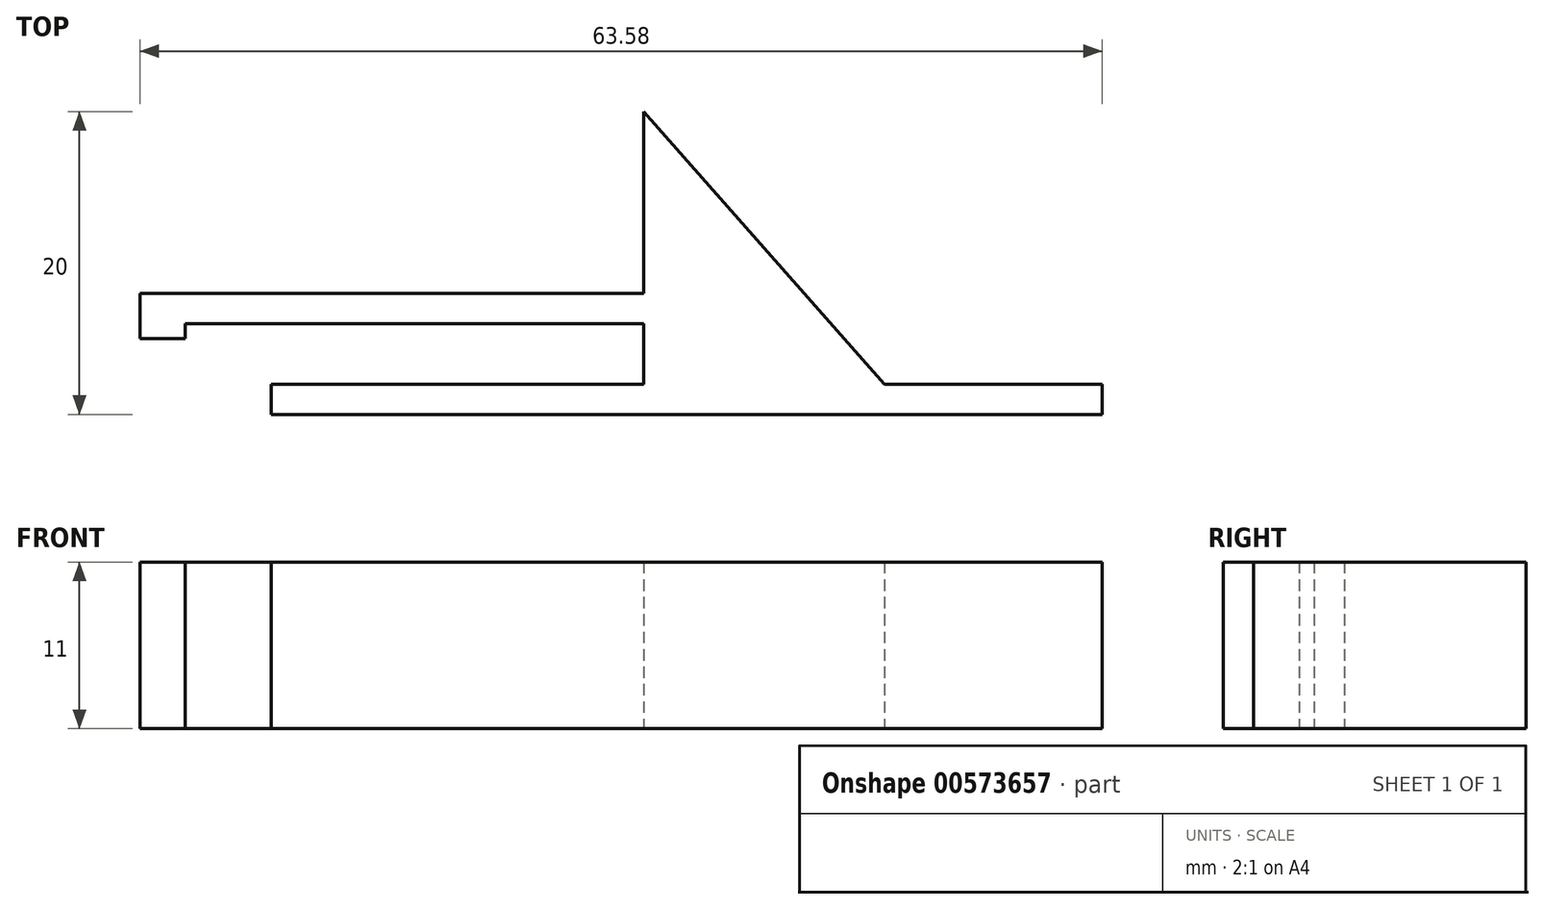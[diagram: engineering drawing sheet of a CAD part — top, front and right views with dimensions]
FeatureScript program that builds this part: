
annotation { "Feature Type Name" : "Feature", "Feature Type Description" : "" }
export const myFeature = defineFeature(function(context is Context, id is Id, definition is map)
    precondition{}
    {
        {
            var Q0;
            Q0=qCreatedBy(makeId("Top.planeOp"),FACE);
            var sketch = newSketch(context, id + "F0", { "sketchPlane" : qUnion([Q0])});
            skLineSegment(sketch, "E0", {"start": v(-24.6, 12.27) * mm, "end": v(30.32, 12.27) * mm});
            skLineSegment(sketch, "E1", {"start": v(30.32, 12.27) * mm, "end": v(30.32, 14.27) * mm});
            skLineSegment(sketch, "E2", {"start": v(30.5, 14.27) * mm, "end": v(15.9, 14.27) * mm});
            skLineSegment(sketch, "E3", {"start": v(-24.6, 12.27) * mm, "end": v(-24.6, 14.27) * mm});
            skLineSegment(sketch, "E4", {"start": v(-24.6, 14.27) * mm, "end": v(0, 14.27) * mm});
            skLineSegment(sketch, "E5", {"start": v(0, 14.27) * mm, "end": v(0, 18.27) * mm});
            skLineSegment(sketch, "E6", {"start": v(0, 18.27) * mm, "end": v(-30.26, 18.27) * mm});
            skLineSegment(sketch, "E7", {"start": v(-30.26, 18.27) * mm, "end": v(-30.26, 17.27) * mm});
            skLineSegment(sketch, "E8", {"start": v(-30.26, 17.27) * mm, "end": v(-33.26, 17.27) * mm});
            skLineSegment(sketch, "E9", {"start": v(-33.26, 17.27) * mm, "end": v(-33.26, 20.27) * mm});
            skLineSegment(sketch, "E10", {"start": v(-33.26, 20.27) * mm, "end": v(0, 20.27) * mm});
            skLineSegment(sketch, "E11", {"start": v(0, 20.27) * mm, "end": v(0, 32.27) * mm});
            skLineSegment(sketch, "E12", {"start": v(0, 32.27) * mm, "end": v(15.9, 14.27) * mm});
            skSolve(sketch);
        }
        {
            var Q0;
            Q0 = qSketchRegion(id + "F0", true);
            extrude(context, id + "F1", {"entities" : qUnion([Q0]), "depth" : 11 * mm, "offsetDistance" : 25 * mm});
        }
    });
